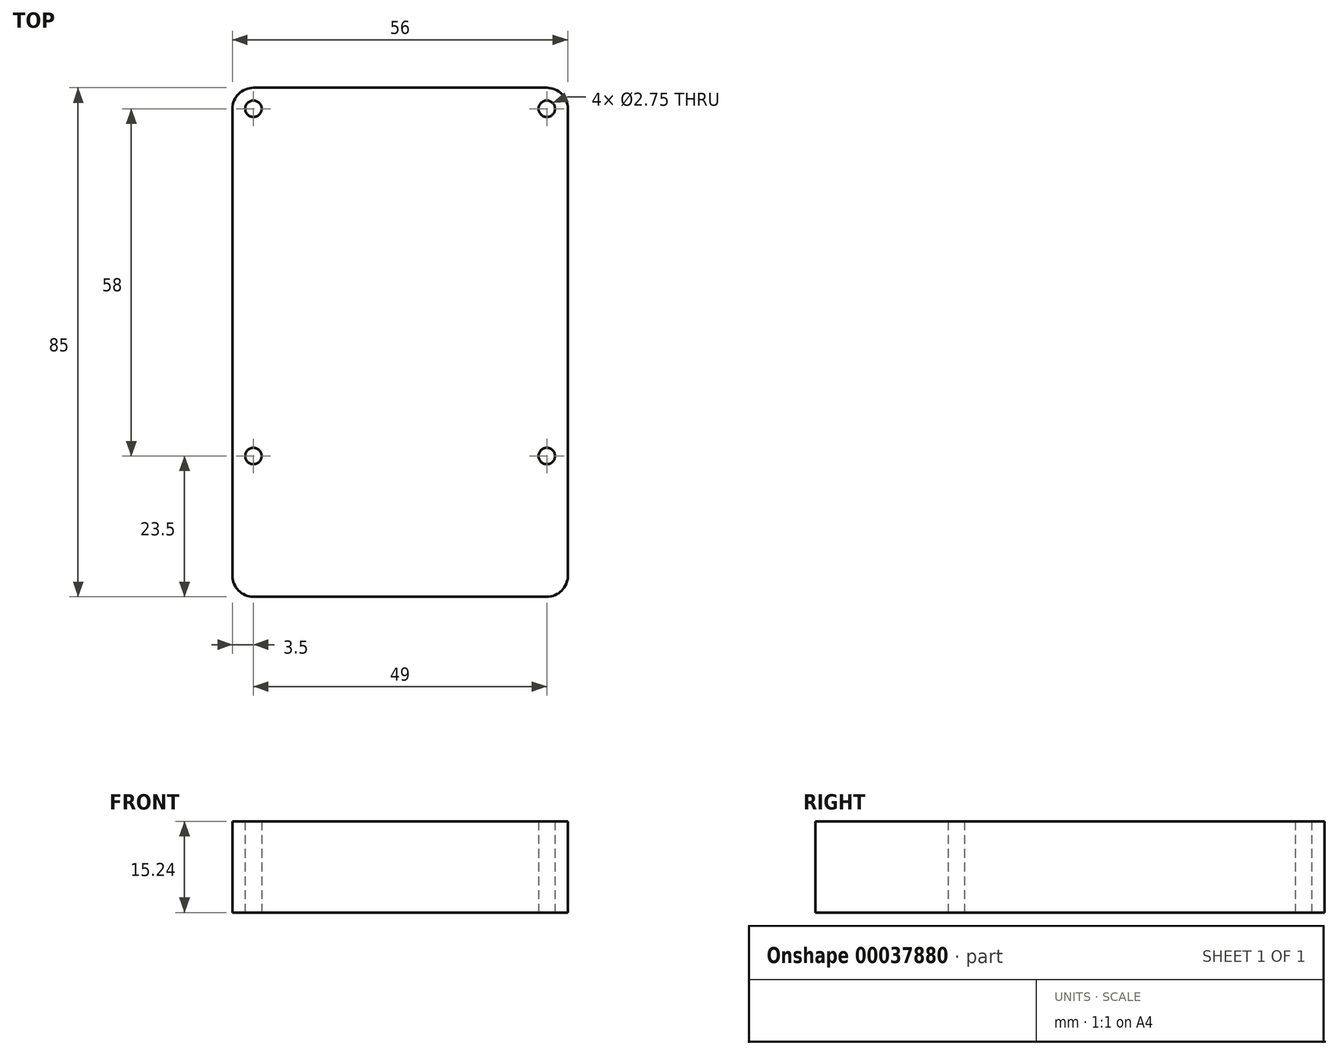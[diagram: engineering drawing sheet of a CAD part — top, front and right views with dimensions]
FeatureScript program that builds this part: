
annotation { "Feature Type Name" : "Feature", "Feature Type Description" : "" }
export const myFeature = defineFeature(function(context is Context, id is Id, definition is map)
    precondition{}
    {
        {
            var Q0;
            Q0=qCreatedBy(makeId("Top.planeOp"),FACE);
            var sketch = newSketch(context, id + "F0", { "sketchPlane" : qUnion([Q0])});
            skLineSegment(sketch, "E0.rect.bottom", {"start": v(24.5, -29) * mm, "end": v(-24.5, -29) * mm, "construction": true});
            skLineSegment(sketch, "E0.rect.top", {"start": v(24.5, 29) * mm, "end": v(-24.5, 29) * mm, "construction": true});
            skLineSegment(sketch, "E0.rect.left", {"start": v(24.5, -29) * mm, "end": v(24.5, 29) * mm, "construction": true});
            skLineSegment(sketch, "E0.rect.right", {"start": v(-24.5, -29) * mm, "end": v(-24.5, 29) * mm, "construction": true});
            skPoint(sketch, "E0.rect.middle", {"position": v(0, 0) * mm});
            skLineSegment(sketch, "E1.bottom", {"start": v(-24.5, 29) * mm, "end": v(-28, 29) * mm, "construction": true});
            skLineSegment(sketch, "E1.left", {"start": v(-24.5, 29) * mm, "end": v(-24.5, 32.5) * mm, "construction": true});
            skLineSegment(sketch, "E2", {"start": v(0, 0) * mm, "end": v(0, -10) * mm, "construction": true});
            skLineSegment(sketch, "E3.rect.bottom", {"start": v(-28, 32.5) * mm, "end": v(28, 32.5) * mm});
            skLineSegment(sketch, "E3.rect.top", {"start": v(-28, -52.5) * mm, "end": v(28, -52.5) * mm});
            skLineSegment(sketch, "E3.rect.left", {"start": v(-28, 32.5) * mm, "end": v(-28, -52.5) * mm});
            skLineSegment(sketch, "E3.rect.right", {"start": v(28, 32.5) * mm, "end": v(28, -52.5) * mm});
            skPoint(sketch, "E3.rect.middle", {"position": v(0, -10) * mm});
            skCircle(sketch, "E4", {"center": v(-24.5, -29) * mm, "radius": 1.37 * mm});
            skCircle(sketch, "E5", {"center": v(24.5, -29) * mm, "radius": 1.37 * mm});
            skCircle(sketch, "E6", {"center": v(24.5, 29) * mm, "radius": 1.37 * mm});
            skCircle(sketch, "E7", {"center": v(-24.5, 29) * mm, "radius": 1.37 * mm});
            skSolve(sketch);
        }
        {
            var Q0;
            Q0 = qSketchRegion(id + "F0", true);
            extrude(context, id + "F1", {"entities" : qUnion([Q0]), "depth" : 15.24 * mm});
        }
        {
            var Q0;
            Q0=makeQuery(id+"F1.opExtrude","SWEPT_EDGE",EDGE,{"disambiguationData":[OSD([sQuery(id+"F0.wireOp",EDGE,"E3.rect.bottom"),sQuery(id+"F0.wireOp",EDGE,"E3.rect.left")])]});
            var Q1;
            Q1=makeQuery(id+"F1.opExtrude","SWEPT_EDGE",EDGE,{"disambiguationData":[OSD([sQuery(id+"F0.wireOp",EDGE,"E3.rect.bottom"),sQuery(id+"F0.wireOp",EDGE,"E3.rect.right")])]});
            var Q2;
            Q2=makeQuery(id+"F1.opExtrude","SWEPT_EDGE",EDGE,{"disambiguationData":[OSD([sQuery(id+"F0.wireOp",EDGE,"E3.rect.top"),sQuery(id+"F0.wireOp",EDGE,"E3.rect.right")])]});
            var Q3;
            Q3=makeQuery(id+"F1.opExtrude","SWEPT_EDGE",EDGE,{"disambiguationData":[OSD([sQuery(id+"F0.wireOp",EDGE,"E3.rect.top"),sQuery(id+"F0.wireOp",EDGE,"E3.rect.left")])]});
            fillet(context, id + "F2", {"entities" : qUnion([Q0, Q1, Q2, Q3]), "radius" : 3.5 * mm, "tangentPropagation" : true, "allowEdgeOverflow" : false});
        }
    });
